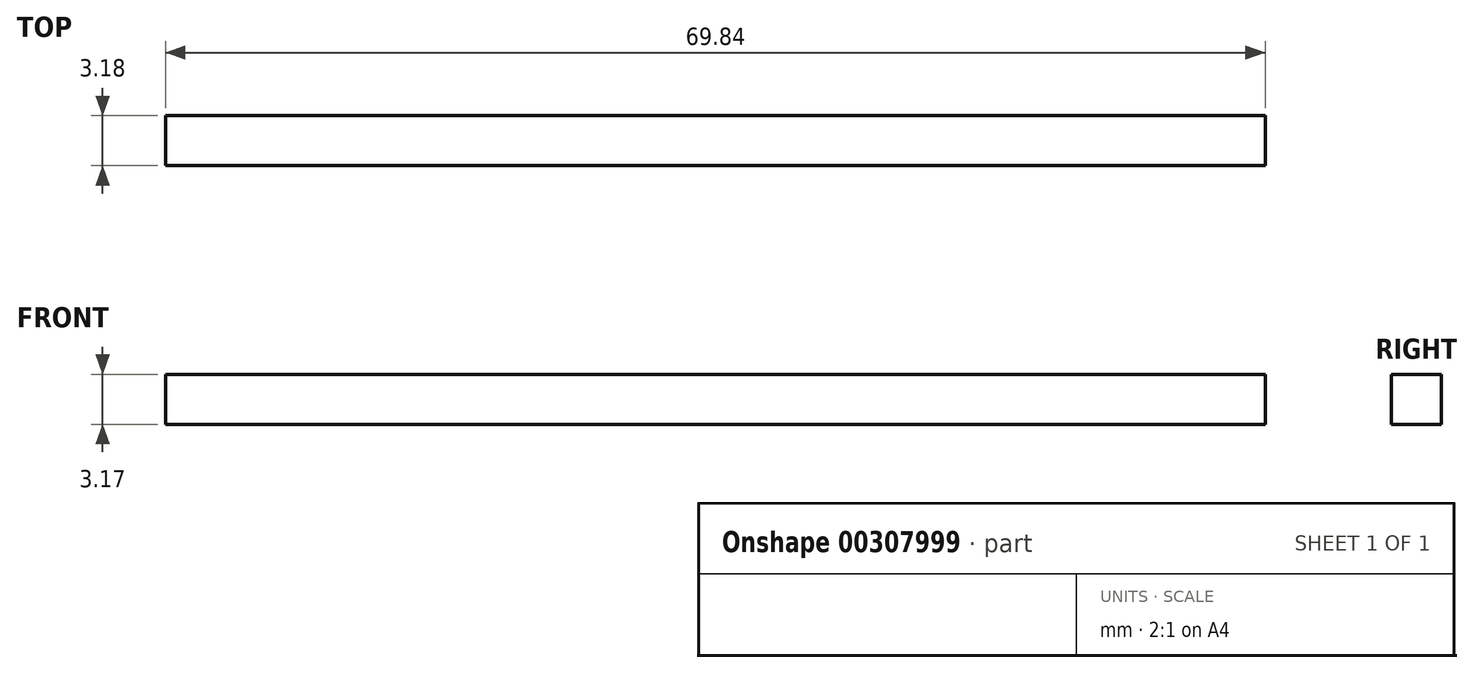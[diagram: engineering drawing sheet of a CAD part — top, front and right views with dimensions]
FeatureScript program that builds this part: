
annotation { "Feature Type Name" : "Feature", "Feature Type Description" : "" }
export const myFeature = defineFeature(function(context is Context, id is Id, definition is map)
    precondition{}
    {
        {
            var Q0;
            Q0=qCreatedBy(makeId("Top.planeOp"),FACE);
            var sketch = newSketch(context, id + "F0", { "sketchPlane" : qUnion([Q0])});
            skLineSegment(sketch, "E0.bottom", {"start": v(34.93, -1.59) * mm, "end": v(-34.93, -1.59) * mm});
            skLineSegment(sketch, "E0.top", {"start": v(34.93, 1.59) * mm, "end": v(-34.93, 1.59) * mm});
            skLineSegment(sketch, "E0.left", {"start": v(34.93, -1.59) * mm, "end": v(34.93, 1.59) * mm});
            skLineSegment(sketch, "E0.right", {"start": v(-34.93, -1.59) * mm, "end": v(-34.93, 1.59) * mm});
            skPoint(sketch, "E0.middle", {"position": v(0, 0) * mm});
            skSolve(sketch);
        }
        {
            var Q0;
            Q0=makeQuery(id+"F0.imprint","IMPRINT",FACE,{"disambiguationData":[TD([[makeQuery(id+"F0.imprint","IMPRINT",EDGE,{"derivedFrom":sQuery(id+"F0.wireOp",EDGE,"E0.bottom")}),-1.0]])]});
            extrude(context, id + "F1", {"entities" : qUnion([Q0]), "depth" : 3.17 * mm});
        }
    });
